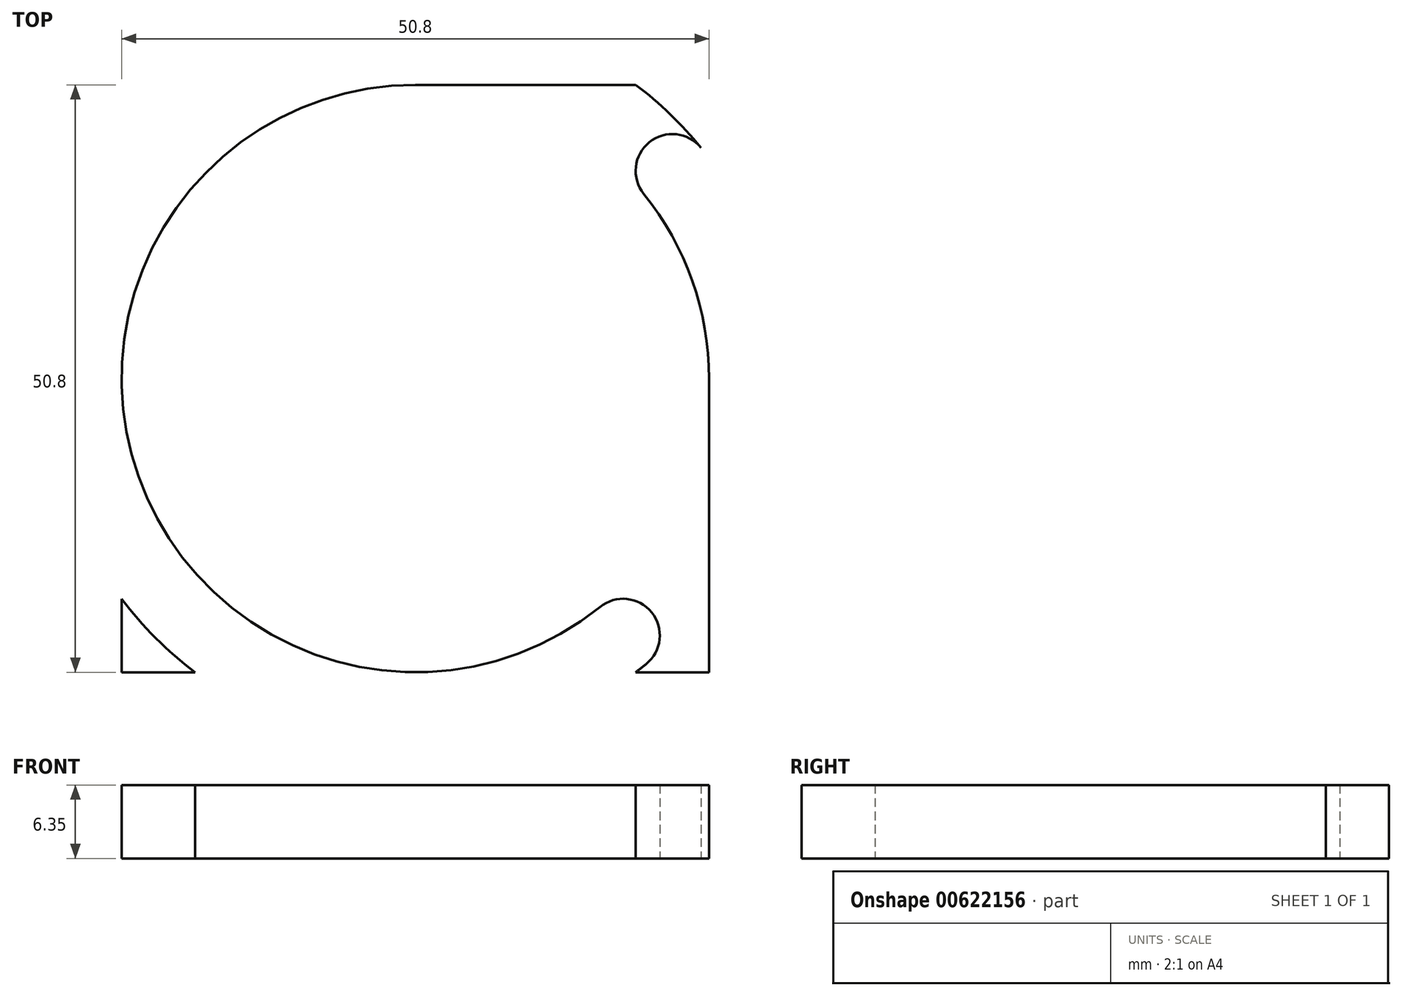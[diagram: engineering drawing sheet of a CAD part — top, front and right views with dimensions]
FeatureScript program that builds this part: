
annotation { "Feature Type Name" : "Feature", "Feature Type Description" : "" }
export const myFeature = defineFeature(function(context is Context, id is Id, definition is map)
    precondition{}
    {
        {
            var Q0;
            Q0=qCreatedBy(makeId("Top.planeOp"),FACE);
            var sketch = newSketch(context, id + "F0", { "sketchPlane" : qUnion([Q0])});
            skLineSegment(sketch, "E0.bottom", {"start": v(25.4, -25.4) * mm, "end": v(-25.4, -25.4) * mm});
            skLineSegment(sketch, "E0.top", {"start": v(25.4, 25.4) * mm, "end": v(-25.4, 25.4) * mm});
            skLineSegment(sketch, "E0.left", {"start": v(25.4, -25.4) * mm, "end": v(25.4, 25.4) * mm});
            skLineSegment(sketch, "E0.right", {"start": v(-25.4, -25.4) * mm, "end": v(-25.4, 25.4) * mm});
            skPoint(sketch, "E0.middle", {"position": v(0, 0) * mm});
            skCircle(sketch, "E1", {"center": v(0, 0) * mm, "radius": 25.4 * mm});
            skCircle(sketch, "E2", {"center": v(-17.96, 22.22) * mm, "radius": 3.18 * mm});
            skCircle(sketch, "E3", {"center": v(22.23, 17.96) * mm, "radius": 3.18 * mm});
            skCircle(sketch, "E4", {"center": v(17.96, -22.23) * mm, "radius": 3.18 * mm});
            skCircle(sketch, "E5", {"center": v(-22.22, -17.96) * mm, "radius": 3.18 * mm});
            skCircle(sketch, "E6", {"center": v(0, 0) * mm, "radius": 31.75 * mm});
            skSolve(sketch);
        }
        {
            var Q0;
            {var subQ0=sQuery(id+"F0.wireOp",EDGE,"E6");var subQ1=sQuery(id+"F0.wireOp",EDGE,"E0.right");var subQ2=makeQuery(id+"F0.imprint","INTERSECT",VERTEX,{"disambiguationData":[OD(1.0)],"derivedFrom":[subQ1,subQ0]});Q0=makeQuery(id+"F0.imprint","IMPRINT",FACE,{"disambiguationData":[TD([[makeQuery(id+"F0.imprint","IMPRINT",EDGE,{"disambiguationData":[TD([[subQ2,1.0]])],"derivedFrom":subQ1}),-1.0]])]});}
            var Q1;
            {var subQ0=sQuery(id+"F0.wireOp",EDGE,"E1");var subQ5=makeQuery(id+"F0.imprint","INTERSECT",VERTEX,{"derivedFrom":[sQuery(id+"F0.wireOp",EDGE,"E0.left"),subQ0]});Q1=makeQuery(id+"F0.imprint","IMPRINT",FACE,{"disambiguationData":[TD([[makeQuery(id+"F0.imprint","IMPRINT",EDGE,{"disambiguationData":[TD([[subQ5,-1.0]])],"derivedFrom":subQ0}),1.0]])]});}
            var Q2;
            {var subQ0=sQuery(id+"F0.wireOp",EDGE,"E6");var subQ1=sQuery(id+"F0.wireOp",EDGE,"E0.left");var subQ2=makeQuery(id+"F0.imprint","INTERSECT",VERTEX,{"disambiguationData":[OD(0.0)],"derivedFrom":[subQ1,subQ0]});Q2=makeQuery(id+"F0.imprint","IMPRINT",FACE,{"disambiguationData":[TD([[makeQuery(id+"F0.imprint","IMPRINT",EDGE,{"disambiguationData":[TD([[subQ2,-1.0]])],"derivedFrom":subQ1}),1.0]])]});}
            var Q3;
            {var subQ0=sQuery(id+"F0.wireOp",EDGE,"E6");var subQ1=sQuery(id+"F0.wireOp",EDGE,"E0.top");var subQ2=makeQuery(id+"F0.imprint","INTERSECT",VERTEX,{"disambiguationData":[OD(0.0)],"derivedFrom":[subQ1,subQ0]});Q3=makeQuery(id+"F0.imprint","IMPRINT",FACE,{"disambiguationData":[TD([[makeQuery(id+"F0.imprint","IMPRINT",EDGE,{"disambiguationData":[TD([[subQ2,-1.0]])],"derivedFrom":subQ1}),1.0]])]});}
            var Q4;
            {var subQ0=sQuery(id+"F0.wireOp",EDGE,"E6");var subQ1=sQuery(id+"F0.wireOp",EDGE,"E0.bottom");var subQ2=makeQuery(id+"F0.imprint","INTERSECT",VERTEX,{"disambiguationData":[OD(1.0)],"derivedFrom":[subQ1,subQ0]});Q4=makeQuery(id+"F0.imprint","IMPRINT",FACE,{"disambiguationData":[TD([[makeQuery(id+"F0.imprint","IMPRINT",EDGE,{"disambiguationData":[TD([[subQ2,1.0]])],"derivedFrom":subQ1}),-1.0]])]});}
            extrude(context, id + "F1", {"entities" : qUnion([Q0, Q1, Q2, Q3, Q4]), "depth" : 6.35 * mm, "offsetDistance" : 25.4 * mm});
        }
    });
